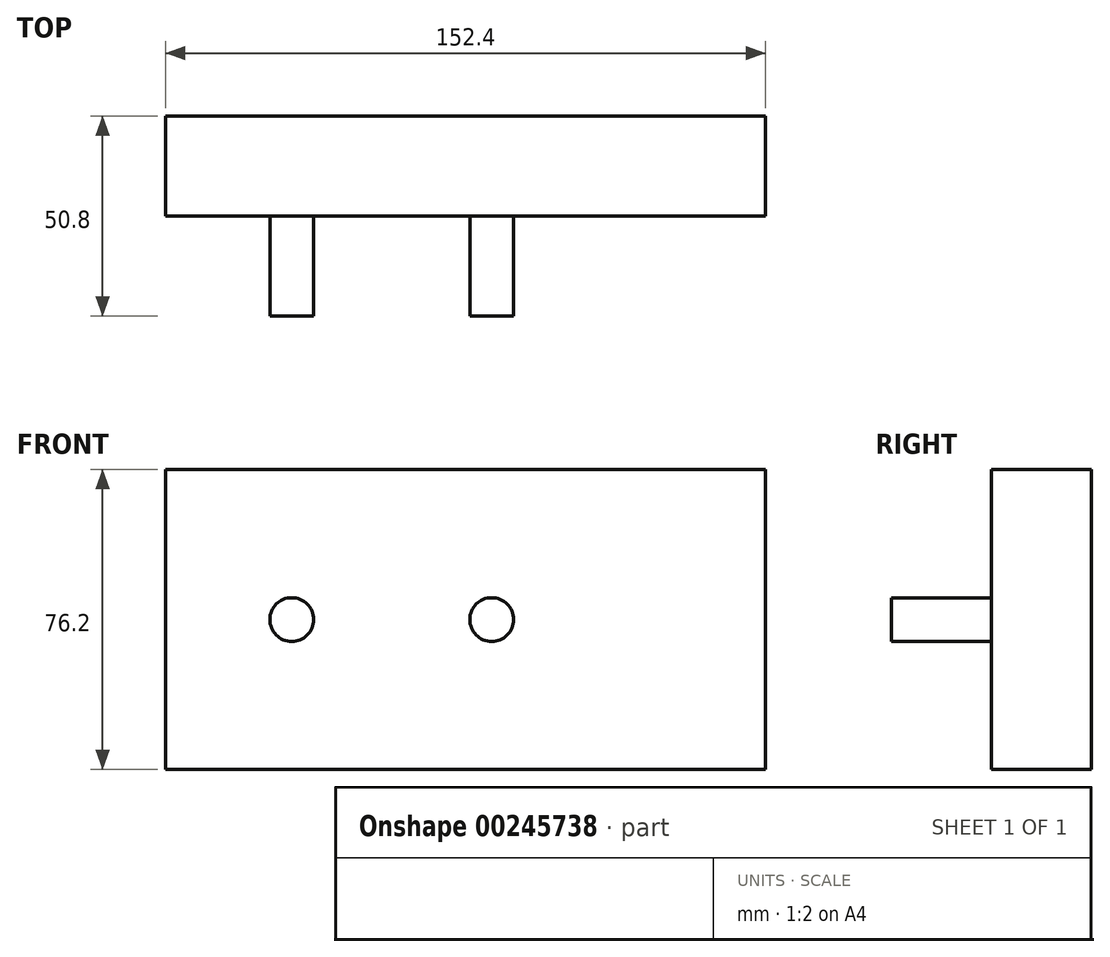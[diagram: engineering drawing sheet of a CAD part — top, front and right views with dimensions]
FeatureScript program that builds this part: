
annotation { "Feature Type Name" : "Feature", "Feature Type Description" : "" }
export const myFeature = defineFeature(function(context is Context, id is Id, definition is map)
    precondition{}
    {
        {
            var Q0;
            Q0=qCreatedBy(makeId("Front.planeOp"),FACE);
            var sketch = newSketch(context, id + "F0", { "sketchPlane" : qUnion([Q0])});
            skLineSegment(sketch, "E0.bottom", {"start": v(0, 0) * mm, "end": v(152.4, 0) * mm});
            skLineSegment(sketch, "E0.top", {"start": v(0, 76.2) * mm, "end": v(152.4, 76.2) * mm});
            skLineSegment(sketch, "E0.left", {"start": v(0, 0) * mm, "end": v(0, 76.2) * mm});
            skLineSegment(sketch, "E0.right", {"start": v(152.4, 0) * mm, "end": v(152.4, 76.2) * mm});
            skSolve(sketch);
        }
        {
            var Q0;
            Q0 = qSketchRegion(id + "F0", true);
            extrude(context, id + "F1", {"entities" : qUnion([Q0]), "depth" : 25.4 * mm});
        }
        {
            var Q0;
            Q0=makeQuery(id+"F1.opExtrude","CAP_FACE",FACE,{"disambiguationData":[OSD([sQuery(id+"F0.wireOp",EDGE,"E0.bottom"),sQuery(id+"F0.wireOp",EDGE,"E0.top"),sQuery(id+"F0.wireOp",EDGE,"E0.left"),sQuery(id+"F0.wireOp",EDGE,"E0.right")])],"isStart":false});
            var sketch = newSketch(context, id + "F2", { "sketchPlane" : qUnion([Q0])});
            skCircle(sketch, "E1", {"center": v(32.05, 38.08) * mm, "radius": 5.56 * mm});
            skLineSegment(sketch, "E2", {"start": v(32.05, 38.08) * mm, "end": v(82.85, 38.08) * mm, "construction": true});
            skCircle(sketch, "E3", {"center": v(82.85, 38.08) * mm, "radius": 5.56 * mm});
            skSolve(sketch);
        }
        {
            var Q0;
            Q0 = qSketchRegion(id + "F2", true);
            extrude(context, id + "F3", {"entities" : qUnion([Q0]), "operationType" : NewBodyOperationType.ADD, "depth" : 25.4 * mm});
        }
    });
